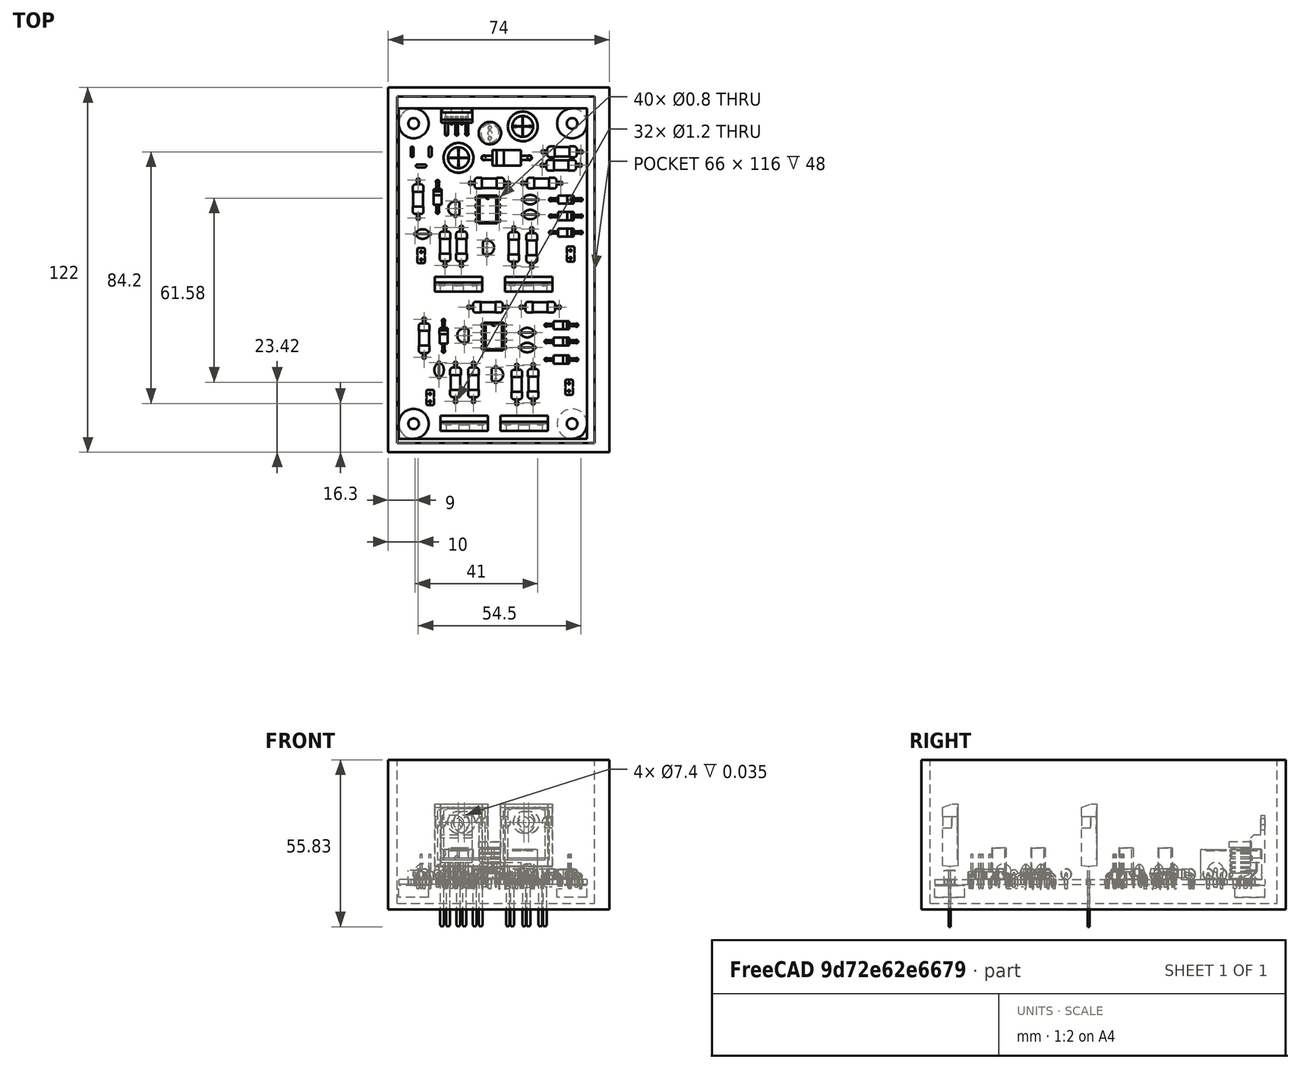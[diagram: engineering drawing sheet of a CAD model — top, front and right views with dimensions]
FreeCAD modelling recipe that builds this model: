
FCSTD DOCUMENT  (FreeCAD 0.18.4R)
Label: electronics_box
License: All rights reserved
LicenseURL: http://en.wikipedia.org/wiki/All_rights_reserved
objects: Part::Feature×50, Part::Cylinder×8, Part::MultiFuse×5, App::Part×4, Part::Box×2, PartDesign::CoordinateSystem×1, Sketcher::SketchObject×1, Part::Cut×1
note: 68 computed .brp shape members not serialized (recipe doc carries the construction recipe); baked Part::Feature solids carry a one-line shape summary decoded from their .brp

FEATURE [PartDesign::CoordinateSystem] Local_CS_ab1c
  AttacherType = Attacher::AttachEngine3D
FEATURE [Part::Feature] Pcb_ab1c
  Placement = pos=(-109,37.5,0) rot=(0,0,1;0rad)
  shape: bbox 63 x 110.5 x 1.6 mm, 149 faces (baked)
FEATURE [Sketcher::SketchObject] PCB_Sketch_ab1c
  sketch-geometry (4):
    g0: LineSegment StartX=-5 StartY=-105.5 StartZ=0 EndX=-5 EndY=5 EndZ=0
    g1: LineSegment StartX=58 StartY=-105.5 StartZ=0 EndX=-5 EndY=-105.5 EndZ=0
    g2: LineSegment StartX=58 StartY=5 StartZ=0 EndX=58 EndY=-105.5 EndZ=0
    g3: LineSegment StartX=-5 StartY=5 StartZ=0 EndX=58 EndY=5 EndZ=0
  constraints (4):
    c: Coincident(g0,g1)
    c: Coincident(g0,g3)
    c: Coincident(g1,g2)
    c: Coincident(g2,g3)
FEATURE [App::Part] Board_Geoms_ab1c
  Group = -> [Local_CS_ab1c,Pcb_ab1c,PCB_Sketch_ab1c]
  Origin = -> Origin
FEATURE [Part::Feature] Shape  label="D4_D_DO-41_SOD81_P10.16mm_Horizontal_60125312"
  Placement = pos=(8,-19.5,0) rot=(0,0,-1;1.5708rad)
  shape: bbox 2.72 x 11.16 x 5.71 mm, 15 faces (baked)
FEATURE [Part::Feature] Shape001  label="C1_C_Disc_D51mm_W32mm_P500mm_60124F99"
  Placement = pos=(8.5,-80,0) rot=(0,0,-1;1.5708rad)
  shape: bbox 3.2 x 5.5 x 7.2 mm, 10 faces (baked)
FEATURE [Part::Feature] Shape002  label="C2_C_Disc_D51mm_W32mm_P500mm_60129F43"
  Placement = pos=(0.5,-37,0) rot=(0,0,1;0rad)
  shape: bbox 5.5 x 3.2 x 7.2 mm, 10 faces (baked)
FEATURE [Part::Feature] Shape003  label="C3_C_Disc_D51mm_W32mm_P500mm_60124FC3"
  Placement = pos=(40.5,-75,0) rot=(0,0,1;3.14159rad)
  shape: bbox 5.5 x 3.2 x 7.2 mm, 10 faces (baked)
FEATURE [Part::Feature] Shape004  label="C4_C_Disc_D51mm_W32mm_P500mm_60124FD8"
  Placement = pos=(41.5,-30.5,0) rot=(0,0,1;3.14159rad)
  shape: bbox 5.5 x 3.2 x 7.2 mm, 10 faces (baked)
FEATURE [Part::Feature] Shape005  label="C5_C_Disc_D51mm_W32mm_P500mm_60124FED"
  Placement = pos=(35.5,-70,0) rot=(0,0,1;0rad)
  shape: bbox 5.5 x 3.2 x 7.2 mm, 10 faces (baked)
FEATURE [Part::Feature] Shape006  label="C6_C_Disc_D51mm_W32mm_P500mm_60125002"
  Placement = pos=(36.5,-25.5,0) rot=(0,0,1;0rad)
  shape: bbox 5.5 x 3.2 x 7.2 mm, 10 faces (baked)
FEATURE [Part::Feature] Shape007  label="C11_CP_Radial_D100mm_P500mm_60125122"
  Placement = pos=(15,-9,0) rot=(0,0,-1;1.5708rad)
  shape: bbox 12.78 x 12.36 x 12 mm, 48 faces (baked)
FEATURE [Part::Feature] Shape008  label="C15_CP_Radial_D100mm_P500mm_6012522D"
  Placement = pos=(34,-1,0) rot=(0,0,1;0rad)
  shape: bbox 12.36 x 12.78 x 12 mm, 48 faces (baked)
FEATURE [Part::Feature] Shape009  label="D1_D_DO-41_SOD81_P10.16mm_Horizontal_601252B5"
  Placement = pos=(54.5,-67.5,0) rot=(0,0,1;3.14159rad)
  shape: bbox 11.16 x 2.72 x 5.71 mm, 15 faces (baked)
FEATURE [Part::Feature] Shape010  label="D2_D_DO-41_SOD81_P10.16mm_Horizontal_601252D4"
  Placement = pos=(56,-25.5,0) rot=(0,0,1;3.14159rad)
  shape: bbox 11.16 x 2.72 x 5.71 mm, 15 faces (baked)
FEATURE [Part::Feature] Shape011  label="D3_D_DO-41_SOD81_P10.16mm_Horizontal_601252F3"
  Placement = pos=(10,-66,0) rot=(0,0,-1;1.5708rad)
  shape: bbox 2.72 x 11.16 x 5.71 mm, 15 faces (baked)
FEATURE [Part::Feature] Shape012  label="D5_D_DO-41_SOD81_P10.16mm_Horizontal_60125331"
  Placement = pos=(54.5,-73,0) rot=(0,0,1;3.14159rad)
  shape: bbox 11.16 x 2.72 x 5.71 mm, 15 faces (baked)
FEATURE [Part::Feature] Shape013  label="D6_D_DO-41_SOD81_P10.16mm_Horizontal_60125350"
  Placement = pos=(56,-31,0) rot=(0,0,1;3.14159rad)
  shape: bbox 11.16 x 2.72 x 5.71 mm, 15 faces (baked)
FEATURE [Part::Feature] Shape014  label="D7_D_DO-41_SOD81_P10.16mm_Horizontal_6012536F"
  Placement = pos=(54.5,-79,0) rot=(0,0,1;3.14159rad)
  shape: bbox 11.16 x 2.72 x 5.71 mm, 15 faces (baked)
FEATURE [Part::Feature] Shape015  label="D8_D_DO-41_SOD81_P10.16mm_Horizontal_6012538E"
  Placement = pos=(56,-36.5,0) rot=(0,0,1;3.14159rad)
  shape: bbox 11.16 x 2.72 x 5.71 mm, 15 faces (baked)
FEATURE [Part::Feature] Shape016  label="D17_D_DO-201AD_P15.24mm_Horizontal_601254A5"
  Placement = pos=(23.5,-11.5,0) rot=(0,0,1;0rad)
  shape: bbox 16.86 x 5.22 x 8.21 mm, 15 faces (baked)
FEATURE [Part::Feature] Shape017  label="J1_PinHeader_1x02_P254mm_Vertical_601255B3"
  Placement = pos=(5.5,-90.5,0) rot=(0,0,1;0rad)
  shape: bbox 2.54 x 5.08 x 11.54 mm, 52 faces (baked)
FEATURE [Part::Feature] Shape018  label="J2_PinHeader_1x02_P254mm_Vertical_601255C9"
  Placement = pos=(2.5,-43,0) rot=(0,0,1;0rad)
  shape: bbox 2.54 x 5.08 x 11.54 mm, 52 faces (baked)
FEATURE [Part::Feature] Shape019  label="J3_PinHeader_1x02_P254mm_Vertical_601255DF"
  Placement = pos=(52,-87,0) rot=(0,0,1;0rad)
  shape: bbox 2.54 x 5.08 x 11.54 mm, 52 faces (baked)
FEATURE [Part::Feature] Shape020  label="J4_PinHeader_1x02_P254mm_Vertical_601255F5"
  Placement = pos=(52.5,-42.5,0) rot=(0,0,1;0rad)
  shape: bbox 2.54 x 5.08 x 11.54 mm, 52 faces (baked)
FEATURE [Part::Feature] Shape021  label="L1_L_Radial_D7.5mm_P3.50mm_Fastron_07P_601256C9"
  Placement = pos=(25.5,-5,0) rot=(0,0,1;1.5708rad)
  shape: bbox 7.644 x 7.644 x 15.55 mm, 27 faces (baked)
FEATURE [Part::Feature] Shape022  label="Q1_TO-247-3_Vertical_601256E1"
  Placement = pos=(31.5,-100.5,0) rot=(0,0,1;0rad)
  shape: bbox 15.9 x 5.03 x 41.1 mm, 64 faces (baked)
FEATURE [Part::Feature] Shape023  label="Q2_TO-247-3_Vertical_601256F9"
  Placement = pos=(33,-54,0) rot=(0,0,1;0rad)
  shape: bbox 15.9 x 5.03 x 41.1 mm, 64 faces (baked)
FEATURE [Part::Feature] Shape024  label="Q7_TO-247-3_Vertical_60125711"
  Placement = pos=(11.5,-100.5,0) rot=(0,0,1;0rad)
  shape: bbox 15.9 x 5.03 x 41.1 mm, 64 faces (baked)
FEATURE [Part::Feature] Shape025  label="Q8_TO-247-3_Vertical_60125729"
  Placement = pos=(9.5,-54,0) rot=(0,0,1;0rad)
  shape: bbox 15.9 x 5.03 x 41.1 mm, 64 faces (baked)
FEATURE [Part::Feature] Shape026  label="R1_R_Axial_DIN0411_L99mm_D36mm_P1270mm_Horizontal_60125800"
  Placement = pos=(40,-93.5,0) rot=(0,0,1;1.5708rad)
  shape: bbox 3.897 x 13.76 x 6.748 mm, 17 faces (baked)
FEATURE [Part::Feature] Shape027  label="R2_R_Axial_DIN0411_L99mm_D36mm_P1270mm_Horizontal_60125817"
  Placement = pos=(39.5,-48,0) rot=(0,0,1;1.5708rad)
  shape: bbox 3.897 x 13.76 x 6.748 mm, 17 faces (baked)
FEATURE [Part::Feature] Shape028  label="R3_R_Axial_DIN0411_L99mm_D36mm_P1270mm_Horizontal_6012582E"
  Placement = pos=(34.5,-81,0) rot=(0,0,-1;1.5708rad)
  shape: bbox 3.897 x 13.76 x 6.748 mm, 17 faces (baked)
FEATURE [Part::Feature] Shape029  label="R4_R_Axial_DIN0411_L99mm_D36mm_P1270mm_Horizontal_60125845"
  Placement = pos=(33.5,-35,0) rot=(0,0,-1;1.5708rad)
  shape: bbox 3.897 x 13.76 x 6.748 mm, 17 faces (baked)
FEATURE [Part::Feature] Shape030  label="R5_R_Axial_DIN0411_L99mm_D36mm_P1270mm_Horizontal_6012585C"
  Placement = pos=(3.5,-65.5,0) rot=(0,0,-1;1.5708rad)
  shape: bbox 3.897 x 13.76 x 6.748 mm, 17 faces (baked)
FEATURE [Part::Feature] Shape031  label="R6_R_Axial_DIN0411_L99mm_D36mm_P1270mm_Horizontal_60125873"
  Placement = pos=(1.5,-19,0) rot=(0,0,-1;1.5708rad)
  shape: bbox 3.897 x 13.76 x 6.748 mm, 17 faces (baked)
FEATURE [Part::Feature] Shape032  label="R7_R_Axial_DIN0411_L99mm_D36mm_P1270mm_Horizontal_6012588A"
  Placement = pos=(20,-93,0) rot=(0,0,1;1.5708rad)
  shape: bbox 3.897 x 13.76 x 6.748 mm, 17 faces (baked)
FEATURE [Part::Feature] Shape033  label="R8_R_Axial_DIN0411_L99mm_D36mm_P1270mm_Horizontal_601258A1"
  Placement = pos=(16,-47.5,0) rot=(0,0,1;1.5708rad)
  shape: bbox 3.897 x 13.76 x 6.748 mm, 17 faces (baked)
FEATURE [Part::Feature] Shape034  label="R9_R_Axial_DIN0411_L99mm_D36mm_P1270mm_Horizontal_601258B8"
  Placement = pos=(18.5,-61.5,0) rot=(0,0,1;0rad)
  shape: bbox 13.76 x 3.897 x 6.748 mm, 17 faces (baked)
FEATURE [Part::Feature] Shape035  label="R10_R_Axial_DIN0411_L99mm_D36mm_P1270mm_Horizontal_601258CF"
  Placement = pos=(19,-20,0) rot=(0,0,1;0rad)
  shape: bbox 13.76 x 3.897 x 6.748 mm, 17 faces (baked)
FEATURE [Part::Feature] Shape036  label="R11_R_Axial_DIN0411_L99mm_D36mm_P1270mm_Horizontal_601258E6"
  Placement = pos=(14,-93,0) rot=(0,0,1;1.5708rad)
  shape: bbox 3.897 x 13.76 x 6.748 mm, 17 faces (baked)
FEATURE [Part::Feature] Shape037  label="R12_R_Axial_DIN0411_L99mm_D36mm_P1270mm_Horizontal_601258FD"
  Placement = pos=(10.5,-47.5,0) rot=(0,0,1;1.5708rad)
  shape: bbox 3.897 x 13.76 x 6.748 mm, 17 faces (baked)
FEATURE [Part::Feature] Shape038  label="R13_R_Axial_DIN0411_L99mm_D36mm_P1270mm_Horizontal_60125914"
  Placement = pos=(36,-61.5,0) rot=(0,0,1;0rad)
  shape: bbox 13.76 x 3.897 x 6.748 mm, 17 faces (baked)
FEATURE [Part::Feature] Shape039  label="R14_R_Axial_DIN0411_L99mm_D36mm_P1270mm_Horizontal_6012592B"
  Placement = pos=(36.5,-20,0) rot=(0,0,1;0rad)
  shape: bbox 13.76 x 3.897 x 6.748 mm, 17 faces (baked)
FEATURE [Part::Feature] Shape040  label="U1_DIP-8_W7.62mm_60125BCB"
  Placement = pos=(23,-67.5,0) rot=(0,0,1;0rad)
  shape: bbox 7.874 x 9.27 x 6.98 mm, 148 faces (baked)
FEATURE [Part::Feature] Shape041  label="U2_DIP-8_W7.62mm_60125BE7"
  Placement = pos=(21,-25,0) rot=(0,0,1;0rad)
  shape: bbox 7.874 x 9.27 x 6.98 mm, 148 faces (baked)
FEATURE [Part::Feature] Shape042  label="Q3_TO-92L_Inline_Wide_6012A555"
  Placement = pos=(17,-73.5,0) rot=(0,0,1;1.5708rad)
  shape: bbox 3.745 x 5.58 x 13.2 mm, 27 faces (baked)
FEATURE [Part::Feature] Shape043  label="Q4_TO-92L_Inline_Wide_6012A569"
  Placement = pos=(14,-31,0) rot=(0,0,1;1.5708rad)
  shape: bbox 3.745 x 5.58 x 13.2 mm, 27 faces (baked)
FEATURE [Part::Feature] Shape044  label="Q5_TO-92L_Inline_Wide_6012A57D"
  Placement = pos=(27.5,-81.5,0) rot=(0,0,-1;1.5708rad)
  shape: bbox 3.745 x 5.58 x 13.2 mm, 27 faces (baked)
FEATURE [Part::Feature] Shape045  label="Q6_TO-92L_Inline_Wide_6012A591"
  Placement = pos=(24.5,-39,0) rot=(0,0,-1;1.5708rad)
  shape: bbox 3.745 x 5.58 x 13.2 mm, 27 faces (baked)
FEATURE [Part::Feature] Shape046  label="R15_R_Axial_DIN0411_L99mm_D36mm_P1270mm_Horizontal_60190BF0"
  Placement = pos=(56,-9.5,0) rot=(0,0,1;3.14159rad)
  shape: bbox 13.76 x 3.897 x 6.748 mm, 17 faces (baked)
FEATURE [Part::Feature] Shape047  label="R16_R_Axial_DIN0411_L99mm_D36mm_P1270mm_Horizontal_60190C07"
  Placement = pos=(43,-14,0) rot=(0,0,1;0rad)
  shape: bbox 13.76 x 3.897 x 6.748 mm, 17 faces (baked)
FEATURE [Part::Feature] Shape048  label="U5_TO_220_5_Pentawatt_Multiwatt_5_Vertical_StaggeredType1_60190C2D"
  Placement = pos=(11,-3.5,0) rot=(0,0,1;0rad)
  shape: bbox 10.4 x 8.75 x 24.4 mm, 89 faces (baked)
FEATURE [App::Part] Top_ab1c
  Group = -> [Shape,Shape001,Shape002,Shape003,Shape004,Shape005,Shape006,Shape007,Shape008,Shape009,Shape010,Shape011,Shape012,Shape013,Shape014,Shape015,Shape016,Shape017,Shape018,Shape019,Shape020,Shape021,Shape022,Shape023,Shape024,Shape025,Shape026,Shape027,Shape028,Shape029,Shape030,Shape031,Shape032,Shape033,Shape034,Shape035,Shape036,Shape037,Shape038,Shape039,Shape040,Shape041,Shape042,Shape043,+5 more]
  Origin = -> Origin003
FEATURE [App::Part] Step_Models_ab1c
  Group = -> [Top_ab1c]
  Origin = -> Origin002
FEATURE [App::Part] Board_ab1c  label="spike_n_hold"
  Group = -> [Board_Geoms_ab1c,Step_Models_ab1c]
  Origin = -> Origin001
FEATURE [Part::Box] Box  label="Cube"
  AttacherType = Attacher::AttachEngine3D
  Height = 50
  Length = 74
  Placement = pos=(-8.5,-110,0) rot=(0,0,1;0rad)
  Width = 122
FEATURE [Part::Cylinder] Cylinder
  Angle = 360
  AttacherType = Attacher::AttachEngine3D
  Height = 8
  Placement = pos=(0,0,5) rot=(0,0,1;0rad)
  Radius = 1.8
FEATURE [Part::Cylinder] Cylinder001
  Angle = 360
  AttacherType = Attacher::AttachEngine3D
  Height = 8
  Placement = pos=(53,0,5) rot=(0,0,1;0rad)
  Radius = 1.8
FEATURE [Part::Cylinder] Cylinder002
  Angle = 360
  AttacherType = Attacher::AttachEngine3D
  Height = 8
  Placement = pos=(53,-100.5,5) rot=(0,0,1;0rad)
  Radius = 1.8
FEATURE [Part::Cylinder] Cylinder003
  Angle = 360
  AttacherType = Attacher::AttachEngine3D
  Height = 8
  Placement = pos=(0,-100.5,5) rot=(0,0,1;0rad)
  Radius = 1.8
FEATURE [Part::Cylinder] Cylinder004
  Angle = 360
  AttacherType = Attacher::AttachEngine3D
  Height = 4
  Placement = pos=(0,0,4) rot=(0,0,1;0rad)
  Radius = 5
FEATURE [Part::Cylinder] Cylinder005
  Angle = 360
  AttacherType = Attacher::AttachEngine3D
  Height = 4
  Placement = pos=(53,0,4) rot=(0,0,1;0rad)
  Radius = 5
FEATURE [Part::Cylinder] Cylinder006
  Angle = 360
  AttacherType = Attacher::AttachEngine3D
  Height = 4
  Placement = pos=(53,-100.5,4) rot=(0,0,1;0rad)
  Radius = 5
FEATURE [Part::Cylinder] Cylinder007
  Angle = 360
  AttacherType = Attacher::AttachEngine3D
  Height = 4
  Placement = pos=(0,-100.5,4) rot=(0,0,1;0rad)
  Radius = 5
FEATURE [Part::Box] Box001  label="Cube001"
  AttacherType = Attacher::AttachEngine3D
  Height = 55
  Length = 66
  Placement = pos=(-5.5,-107,2) rot=(0,0,1;0rad)
  Width = 116
FEATURE [Part::MultiFuse] Fusion
  Shapes = -> [Cylinder,Cylinder004]
FEATURE [Part::MultiFuse] Fusion001
  Shapes = -> [Cylinder005,Cylinder001]
FEATURE [Part::MultiFuse] Fusion002
  Shapes = -> [Cylinder002,Cylinder006]
FEATURE [Part::MultiFuse] Fusion003
  Shapes = -> [Cylinder003,Cylinder007]
FEATURE [Part::Cut] Cut
  Base = -> Box
  Tool = -> Box001
FEATURE [Part::MultiFuse] Fusion004
  Placement = pos=(0,0,-10) rot=(0,0,1;0rad)
  Shapes = -> [Cut,Fusion,Fusion001,Fusion002,Fusion003]
